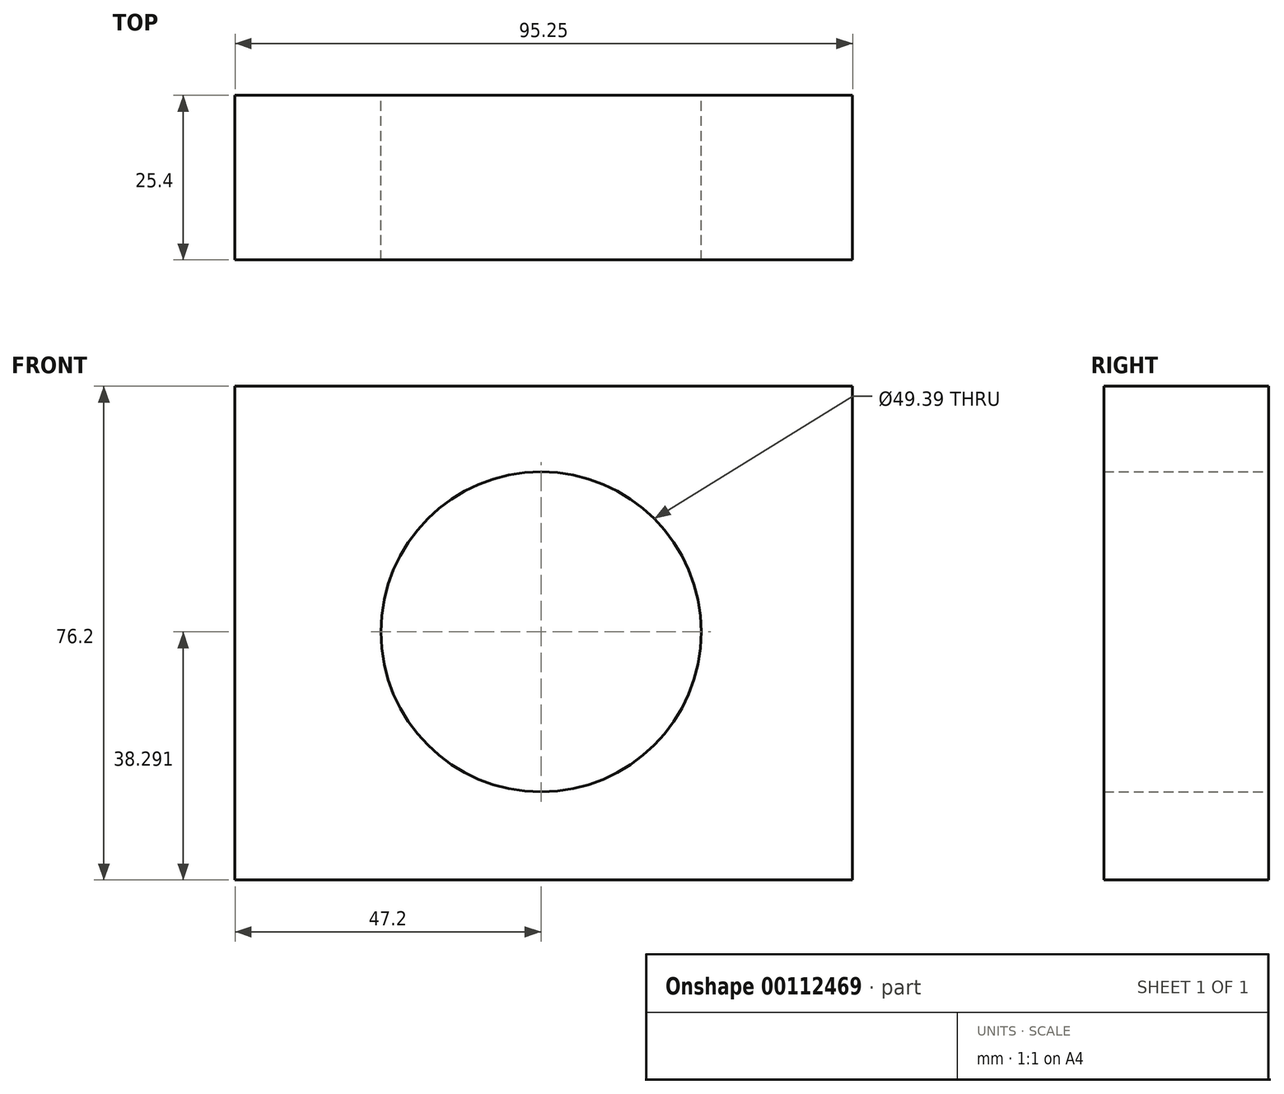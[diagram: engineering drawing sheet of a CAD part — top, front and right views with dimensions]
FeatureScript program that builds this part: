
annotation { "Feature Type Name" : "Feature", "Feature Type Description" : "" }
export const myFeature = defineFeature(function(context is Context, id is Id, definition is map)
    precondition{}
    {
        {
            var Q0;
            Q0=qCreatedBy(makeId("Front.planeOp"),FACE);
            var sketch = newSketch(context, id + "F0", { "sketchPlane" : qUnion([Q0])});
            skLineSegment(sketch, "E0", {"start": v(-66.56, 0) * mm, "end": v(-66.56, 76.2) * mm});
            skLineSegment(sketch, "E1", {"start": v(-66.56, 76.2) * mm, "end": v(28.69, 76.2) * mm});
            skLineSegment(sketch, "E2", {"start": v(28.69, 76.2) * mm, "end": v(28.69, 0) * mm});
            skLineSegment(sketch, "E3", {"start": v(28.69, 0) * mm, "end": v(-66.56, 0) * mm});
            skCircle(sketch, "E4", {"center": v(-19.36, 38.3) * mm, "radius": 24.7 * mm});
            skSolve(sketch);
        }
        {
            var Q0;
            Q0=makeQuery(id+"F0.imprint","IMPRINT",FACE,{"disambiguationData":[TD([[makeQuery(id+"F0.imprint","IMPRINT",EDGE,{"derivedFrom":sQuery(id+"F0.wireOp",EDGE,"E0")}),-1.0]])]});
            extrude(context, id + "F1", {"entities" : qUnion([Q0]), "depth" : 25.4 * mm});
        }
    });
